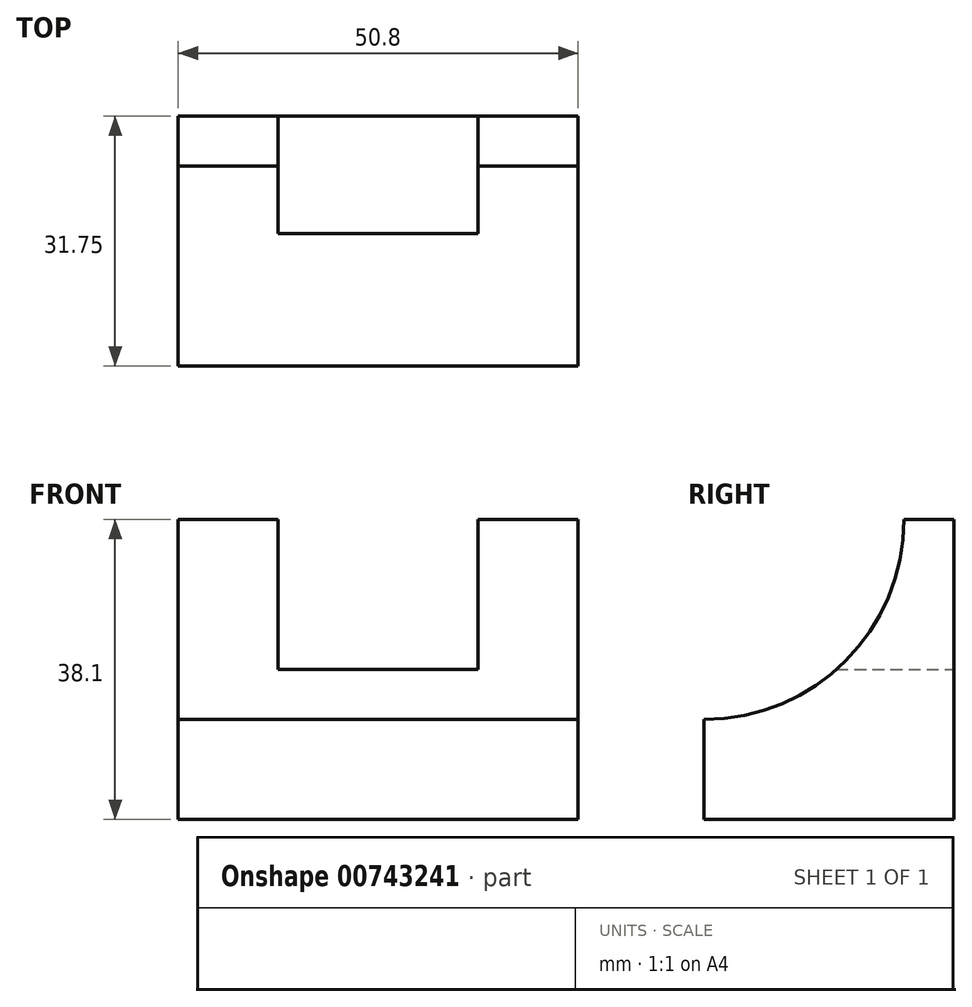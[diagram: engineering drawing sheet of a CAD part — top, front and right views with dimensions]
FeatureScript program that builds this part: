
annotation { "Feature Type Name" : "Feature", "Feature Type Description" : "" }
export const myFeature = defineFeature(function(context is Context, id is Id, definition is map)
    precondition{}
    {
        {
            var Q0;
            Q0=qCreatedBy(makeId("Front.planeOp"),FACE);
            var sketch = newSketch(context, id + "F0", { "sketchPlane" : qUnion([Q0])});
            skLineSegment(sketch, "E0.bottom", {"start": v(0, 0) * mm, "end": v(50.8, 0) * mm});
            skLineSegment(sketch, "E0.top", {"start": v(0, 38.1) * mm, "end": v(50.8, 38.1) * mm});
            skLineSegment(sketch, "E0.left", {"start": v(0, 0) * mm, "end": v(0, 38.1) * mm});
            skLineSegment(sketch, "E0.right", {"start": v(50.8, 0) * mm, "end": v(50.8, 38.1) * mm});
            skSolve(sketch);
        }
        {
            var Q0;
            Q0=makeQuery(id+"F0.imprint","IMPRINT",FACE,{"disambiguationData":[TD([[makeQuery(id+"F0.imprint","IMPRINT",EDGE,{"derivedFrom":sQuery(id+"F0.wireOp",EDGE,"E0.bottom")}),1.0]])]});
            extrude(context, id + "F1", {"entities" : qUnion([Q0]), "depth" : 31.75 * mm, "offsetDistance" : 25.4 * mm});
        }
        {
            var Q0;
            Q0=makeQuery(id+"F1.opExtrude","SWEPT_FACE",FACE,{"disambiguationData":[OSD([sQuery(id+"F0.wireOp",EDGE,"E0.right")])]});
            var sketch = newSketch(context, id + "F2", { "sketchPlane" : qUnion([Q0])});
            skCircle(sketch, "E1", {"center": v(-31.75, 38.1) * mm, "radius": 25.4 * mm});
            skSolve(sketch);
        }
        {
            var Q0;
            {var subQ0=sQuery(id+"F2.wireOp",EDGE,"E1");var subQ1=sQuery(id+"F0.wireOp",EDGE,"E0.right");var subQ4=makeQuery(id+"F1.opExtrude","CAP_EDGE",EDGE,{"disambiguationData":[OSD([subQ1])],"isStart":false});var subQ5=makeQuery(id+"F2.imprint","INTERSECT",VERTEX,{"derivedFrom":[subQ4,subQ0]});Q0=makeQuery(id+"F2.imprint","IMPRINT",FACE,{"disambiguationData":[TD([[makeQuery(id+"F2.imprint","IMPRINT",EDGE,{"disambiguationData":[TD([[subQ5,-1.0]])],"derivedFrom":subQ0}),1.0]])]});}
            extrude(context, id + "F3", {"entities" : qUnion([Q0]), "operationType" : NewBodyOperationType.REMOVE, "oppositeDirection" : true, "depth" : 50.8 * mm, "offsetDistance" : 25.4 * mm});
        }
        {
            var Q0;
            Q0=makeQuery(id+"F1.opExtrude","CAP_FACE",FACE,{"disambiguationData":[OSD([sQuery(id+"F0.wireOp",EDGE,"E0.bottom"),sQuery(id+"F0.wireOp",EDGE,"E0.top"),sQuery(id+"F0.wireOp",EDGE,"E0.left"),sQuery(id+"F0.wireOp",EDGE,"E0.right")])],"isStart":true});
            var sketch = newSketch(context, id + "F4", { "sketchPlane" : qUnion([Q0])});
            skLineSegment(sketch, "E2.bottom", {"start": v(-38.1, 38.1) * mm, "end": v(-12.7, 38.1) * mm});
            skLineSegment(sketch, "E2.top", {"start": v(-38.1, 19.05) * mm, "end": v(-12.7, 19.05) * mm});
            skLineSegment(sketch, "E2.left", {"start": v(-38.1, 38.1) * mm, "end": v(-38.1, 19.05) * mm});
            skLineSegment(sketch, "E2.right", {"start": v(-12.7, 38.1) * mm, "end": v(-12.7, 19.05) * mm});
            skSolve(sketch);
        }
        {
            var Q0;
            Q0=makeQuery(id+"F4.imprint","IMPRINT",FACE,{"disambiguationData":[TD([[makeQuery(id+"F4.imprint","IMPRINT",EDGE,{"derivedFrom":sQuery(id+"F4.wireOp",EDGE,"E2.bottom")}),1.0]])]});
            extrude(context, id + "F5", {"entities" : qUnion([Q0]), "operationType" : NewBodyOperationType.REMOVE, "oppositeDirection" : true, "depth" : 25.4 * mm, "offsetDistance" : 25.4 * mm});
        }
    });
